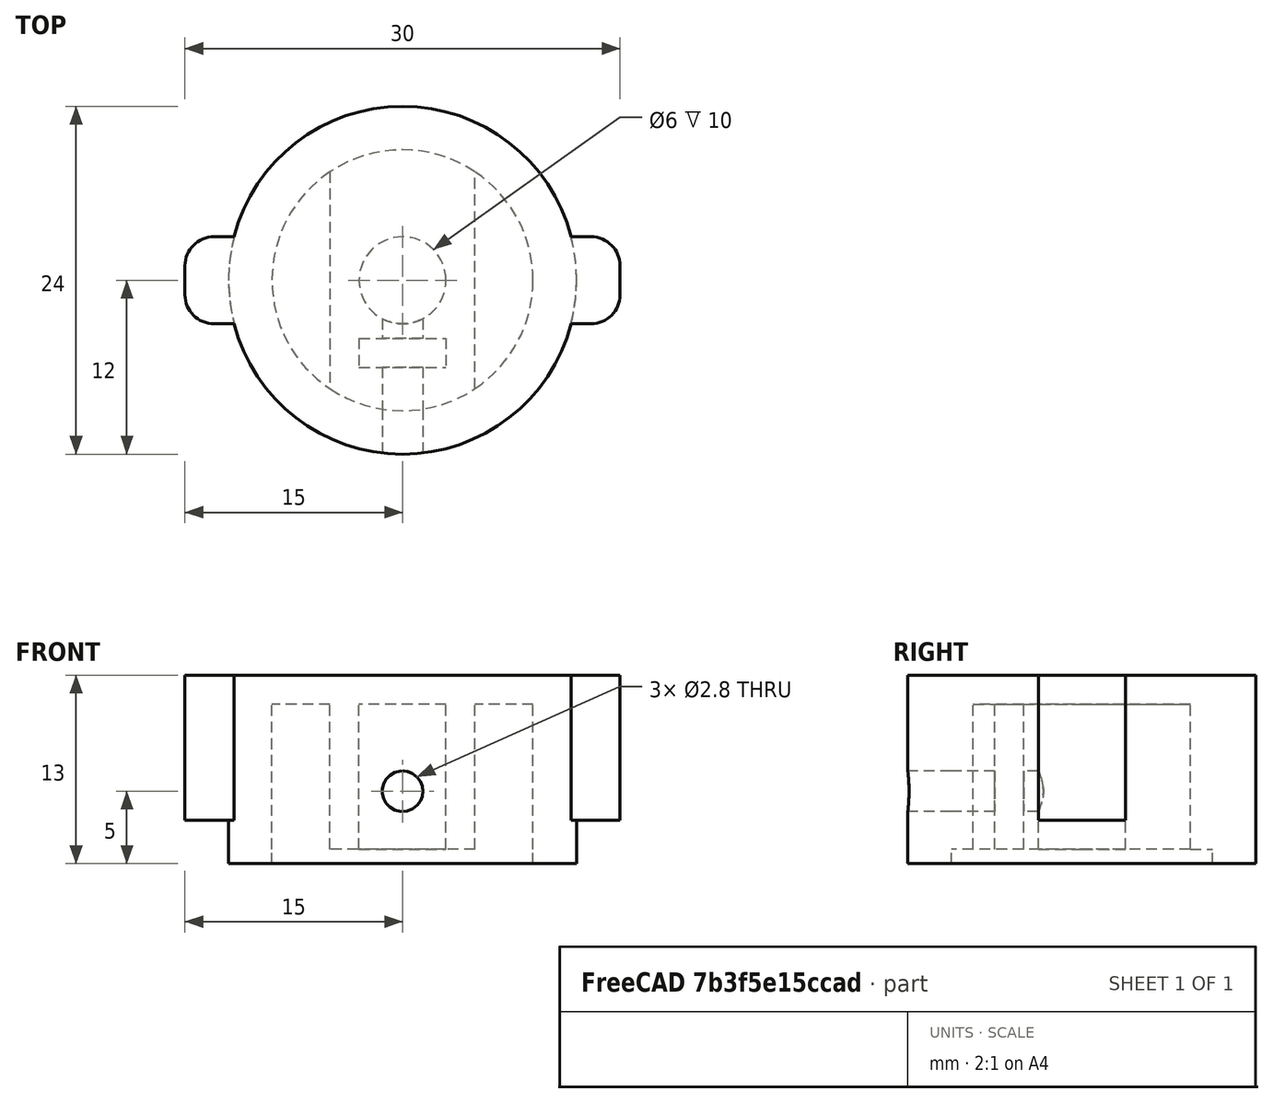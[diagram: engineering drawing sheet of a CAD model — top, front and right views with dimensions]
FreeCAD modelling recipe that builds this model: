
FCSTD DOCUMENT  (FreeCAD 0.18.4R)
Label: manopola-cappa-guido
License: All rights reserved
LicenseURL: http://en.wikipedia.org/wiki/All_rights_reserved
objects: Part::Cylinder×6, Part::Cut×6, Part::Box×4, Part::MultiFuse×2, Part::Fillet×2, Part::Part2DObjectPython×1
note: 21 computed .brp shape members not serialized (recipe doc carries the construction recipe); baked Part::Feature solids carry a one-line shape summary decoded from their .brp

FEATURE [Part::Cylinder] Cylinder
  Angle = 360
  AttacherType = Attacher::AttachEngine3D
  Height = 13
  Radius = 12
FEATURE [Part::Cylinder] Cylinder001
  Angle = 360
  AttacherType = Attacher::AttachEngine3D
  Height = 11
  Radius = 9
FEATURE [Part::Cut] Cut
  Base = -> Cylinder
  Tool = -> Cylinder001
FEATURE [Part::Box] Box  label="Cube"
  AttacherType = Attacher::AttachEngine3D
  Height = 12
  Length = 10
  Placement = pos=(-5,-10,0) rot=(0,0,1;0rad)
  Width = 20
FEATURE [Part::Cylinder] Cylinder002
  Angle = 360
  AttacherType = Attacher::AttachEngine3D
  Height = 12
  Radius = 3
FEATURE [Part::Box] Box001  label="Cube001"
  AttacherType = Attacher::AttachEngine3D
  Height = 12
  Length = 6
  Placement = pos=(-3,-6,0) rot=(0,0,1;0rad)
  Width = 2
FEATURE [Part::Cut] Cut001
  Base = -> Box
  Tool = -> Cylinder002
FEATURE [Part::Cut] Cut002
  Base = -> Cut001
  Tool = -> Box001
FEATURE [Part::Cylinder] Cylinder003
  Angle = 360
  AttacherType = Attacher::AttachEngine3D
  Height = 11
  Placement = pos=(0,-2,5) rot=(1,0,0;1.5708rad)
  Radius = 1.4
FEATURE [Part::Cut] Cut003
  Base = -> Cut002
  Tool = -> Cylinder003
FEATURE [Part::Cylinder] Cylinder004
  Angle = 360
  AttacherType = Attacher::AttachEngine3D
  Height = 1
  Radius = 9
FEATURE [Part::MultiFuse] Fusion
  Shapes = -> [Cut,Cut003]
FEATURE [Part::Cut] Cut004
  Base = -> Fusion
  Tool = -> Cylinder004
FEATURE [Part::Cylinder] Cylinder005
  Angle = 360
  AttacherType = Attacher::AttachEngine3D
  Height = 11
  Placement = pos=(0,-2,5) rot=(1,0,0;1.5708rad)
  Radius = 1.4
FEATURE [Part::Cut] Cut005
  Base = -> Cut004
  Tool = -> Cylinder005
FEATURE [Part::Part2DObjectPython] InvoluteGear  # Draft 2D object (typed FeaturePython)
  ExternalGear = true
  HighPrecision = true
  Modules = 0.9
  NumberOfTeeth = 26
  PressureAngle = 20
FEATURE [Part::Box] Box002  label="Cube002"
  AttacherType = Attacher::AttachEngine3D
  Height = 10
  Length = 5
  Placement = pos=(10,-3,3) rot=(0,0,1;0rad)
  Width = 6
FEATURE [Part::Box] Box003  label="Cube003"
  AttacherType = Attacher::AttachEngine3D
  Height = 10
  Length = 5
  Placement = pos=(-15,-3,3) rot=(0,0,1;0rad)
  Width = 6
FEATURE [Part::Fillet] Fillet
  Base = -> Box003
  Edges = 2 edges r=2: [Edge1,Edge3]
FEATURE [Part::Fillet] Fillet001
  Base = -> Box002
  Edges = 2 edges r=2: [Edge5,Edge7]
FEATURE [Part::MultiFuse] Fusion001
  Shapes = -> [Cut005,Fillet,Fillet001]
